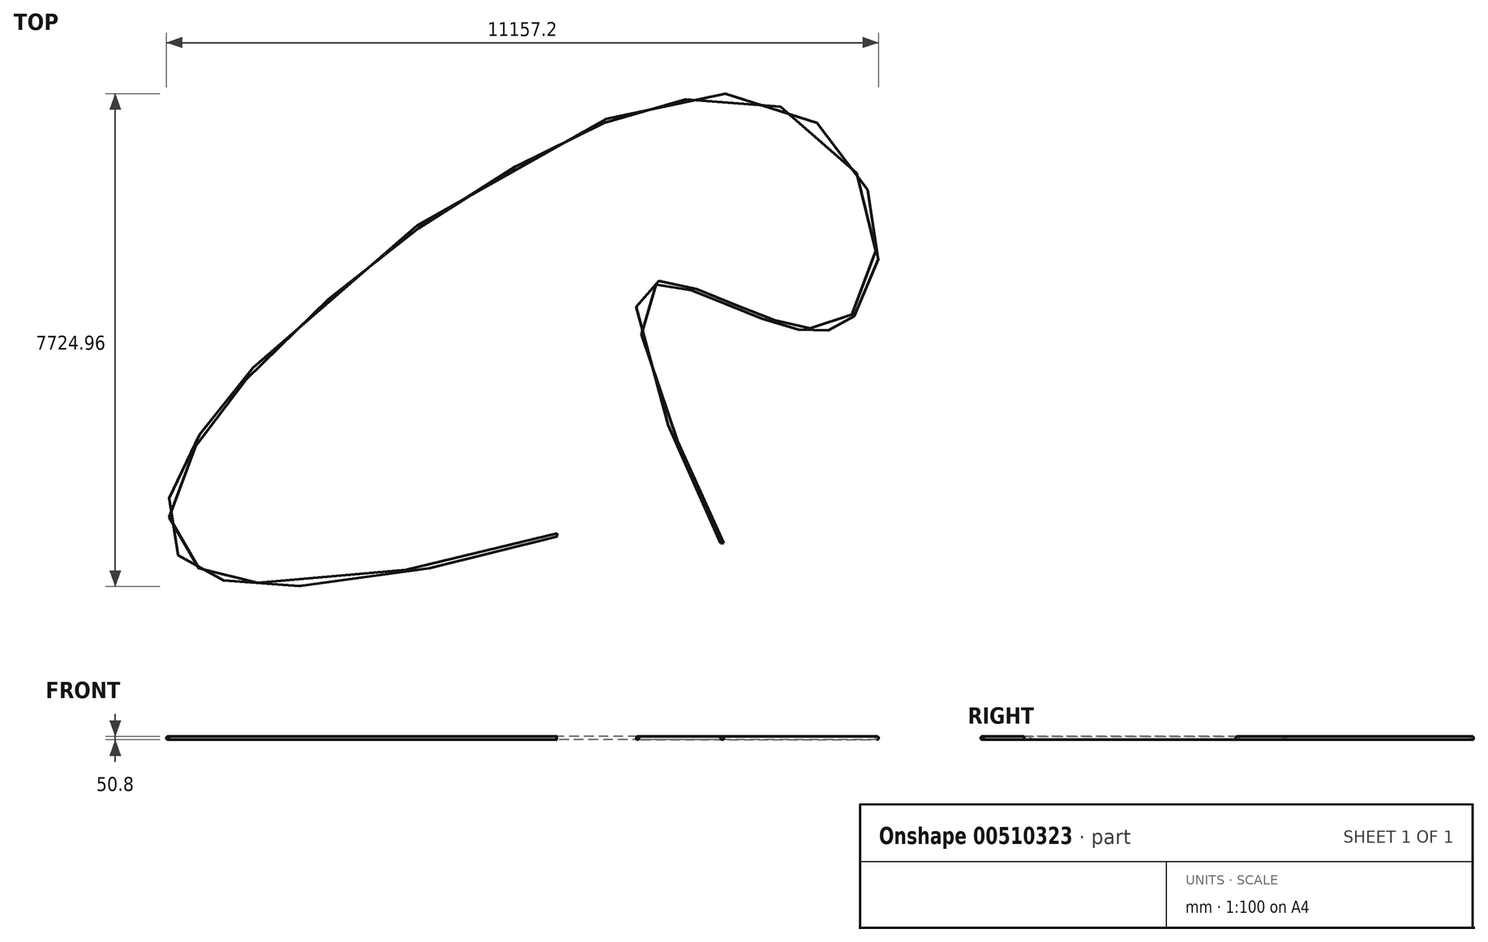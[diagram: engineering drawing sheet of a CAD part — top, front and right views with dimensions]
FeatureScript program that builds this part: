
annotation { "Feature Type Name" : "Feature", "Feature Type Description" : "" }
export const myFeature = defineFeature(function(context is Context, id is Id, definition is map)
    precondition{}
    {
        {
            var Q0;
            Q0=qCreatedBy(makeId("Front.planeOp"),FACE);
            var sketch = newSketch(context, id + "F0", { "sketchPlane" : qUnion([Q0])});
            skCircle(sketch, "E0", {"center": v(0, 2.74) * mm, "radius": 25.4 * mm});
            skSolve(sketch);
        }
        {
            var Q0;
            Q0=qCreatedBy(makeId("Top.planeOp"),FACE);
            var sketch = newSketch(context, id + "F1", { "sketchPlane" : qUnion([Q0])});
            skFitSpline(sketch, "E1", {"points": [v(0, 0) * mm, v(1557.2, 3344.37) * mm, v(-891.67, 6917.39) * mm, v(-2589.5, 125.41) * mm], "startDerivative": vector(-32603.12, 68208.19) * mm, "endDerivative": vector(93200, 26272.47) * mm});
            skSolve(sketch);
        }
        {
            var Q0;
            Q0=makeQuery(id+"F0.imprint","IMPRINT",FACE,{"disambiguationData":[TD([[makeQuery(id+"F0.imprint","IMPRINT",EDGE,{"derivedFrom":sQuery(id+"F0.wireOp",EDGE,"E0")}),1.0]])]});
            var Q1;
            Q1=sQuery(id+"F1.wireOp",EDGE,"E1");
            sweep(context, id + "F2", {"profiles" : qUnion([Q0]), "path" : qUnion([Q1])});
        }
    });
